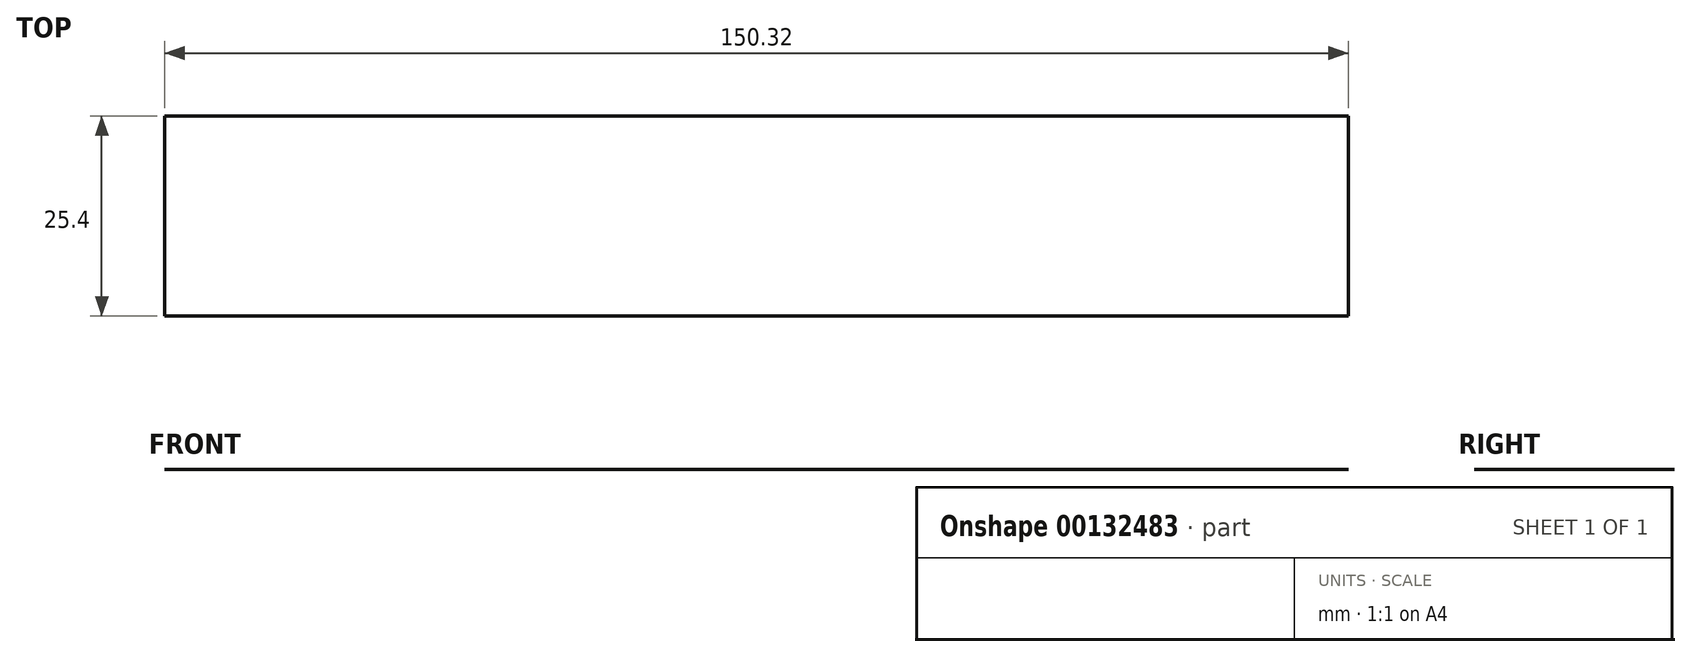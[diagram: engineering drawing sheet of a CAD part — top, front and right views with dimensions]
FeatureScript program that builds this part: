
annotation { "Feature Type Name" : "Feature", "Feature Type Description" : "" }
export const myFeature = defineFeature(function(context is Context, id is Id, definition is map)
    precondition{}
    {
        {
            var Q0;
            Q0=qCreatedBy(makeId("Front.planeOp"),FACE);
            var sketch = newSketch(context, id + "F0", { "sketchPlane" : qUnion([Q0])});
            skLineSegment(sketch, "E0", {"start": v(-75.89, 0) * mm, "end": v(-75.89, 76.1) * mm});
            skLineSegment(sketch, "E1", {"start": v(76.5, 76.1) * mm, "end": v(76.5, -76.3) * mm});
            skLineSegment(sketch, "E2", {"start": v(76.5, -76.3) * mm, "end": v(-76.71, -76.3) * mm});
            skLineSegment(sketch, "E3", {"start": v(-76.71, -76.3) * mm, "end": v(-75.89, 1.65) * mm});
            skLineSegment(sketch, "E4", {"start": v(-75.89, 1.65) * mm, "end": v(-75.89, 76.1) * mm});
            skLineSegment(sketch, "E5", {"start": v(76.5, 76.1) * mm, "end": v(-73.82, 76.1) * mm});
            skSolve(sketch);
        }
        {
            var Q0;
            Q0=sQuery(id+"F0.wireOp",EDGE,"E5");
            extrude(context, id + "F1", {"bodyType" : ToolBodyType.SURFACE, "surfaceEntities" : qUnion([Q0]), "depth" : 25.4 * mm});
        }
    });
